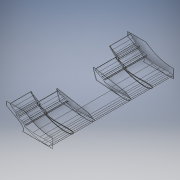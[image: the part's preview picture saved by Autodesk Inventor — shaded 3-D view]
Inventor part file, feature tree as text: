
AUTODESK INVENTOR PART (.ipt)
format: ipt  version: 2018.2 (Build 222227000, 227)  size: 755,200 bytes
history: native  units: mm
features: projected_geometry x11, extrude x8, sketch x8, mirror x1, other x1
ambient origin geometry x8: Origin, YZ Plane, XZ Plane, XY Plane, X Axis, Y Axis, Z Axis, Center Point
bodies: Body1 (feature_tree)
feature tree (29):
  extrude  "押し出し7"  Depth=394.0mm TaperAngle=0.0deg
  extrude  "押し出し8"  Depth=5.0mm TaperAngle=0.0deg
  extrude  "押し出し9"  Depth=225.0mm TaperAngle=0.0deg
  extrude  "押し出し10"  Depth=5.0mm TaperAngle=0.0deg
  extrude  "押し出し11"  Depth=225.0mm TaperAngle=0.0deg
  extrude  "押し出し12"  Depth=2.0mm TaperAngle=0.0deg
  extrude  "押し出し13"  Depth=2.0mm
  extrude  "押し出し14"  Depth=5.0mm
  mirror  "ミラー2"
  other  "ソリッド36"
  sketch  "スケッチ8"
  projected_geometry  "投影ループ7"
  sketch  "スケッチ9"
  projected_geometry  "投影ループ8"
  sketch  "スケッチ10"
  projected_geometry  "投影ループ9"
  projected_geometry  "投影ループ10"
  sketch  "スケッチ11"
  projected_geometry  "投影ループ11"
  sketch  "スケッチ12"
  projected_geometry  "投影ループ12"
  projected_geometry  "投影ループ13"
  projected_geometry  "投影ループ14"
  sketch  "スケッチ13"
  projected_geometry  "投影ループ15"
  sketch  "スケッチ14"
  projected_geometry  "投影ループ16"
  sketch  "スケッチ15"
  projected_geometry  "投影ループ17"
